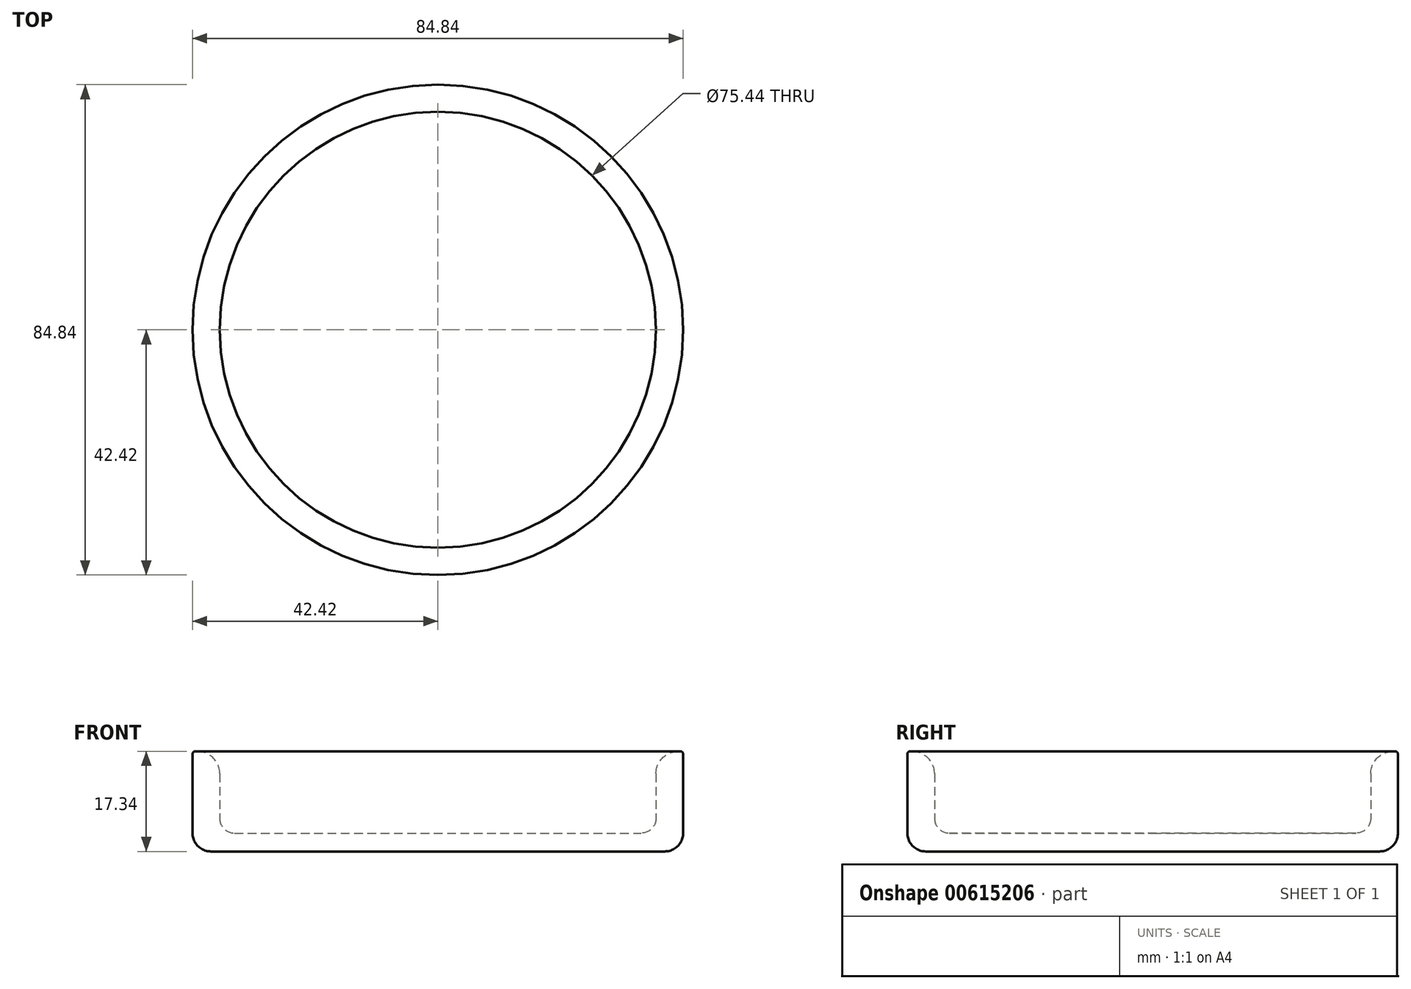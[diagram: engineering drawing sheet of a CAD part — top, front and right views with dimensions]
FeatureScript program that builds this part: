
annotation { "Feature Type Name" : "Feature", "Feature Type Description" : "" }
export const myFeature = defineFeature(function(context is Context, id is Id, definition is map)
    precondition{}
    {
        {
            var Q0;
            Q0=qCreatedBy(makeId("Front.planeOp"),FACE);
            var sketch = newSketch(context, id + "F0", { "sketchPlane" : qUnion([Q0])});
            skLineSegment(sketch, "E0", {"start": v(0, 0) * mm, "end": v(0, 3.18) * mm});
            skLineSegment(sketch, "E1", {"start": v(0, 3.18) * mm, "end": v(35.18, 3.18) * mm});
            skLineSegment(sketch, "E2", {"start": v(37.72, 5.72) * mm, "end": v(37.72, 13.47) * mm});
            skLineSegment(sketch, "E3", {"start": v(41.12, 17.26) * mm, "end": v(41.86, 17.34) * mm});
            skLineSegment(sketch, "E4", {"start": v(42.42, 16.83) * mm, "end": v(42.42, 3.18) * mm});
            skLineSegment(sketch, "E5", {"start": v(39.24, 0) * mm, "end": v(0, 0) * mm});
            skPoint(sketch, "E6.visualSharp", {"position": v(37.72, 3.18) * mm});
            skArc(sketch, "E6.filletArc", {"start": v(35.18, 3.18) * mm, "mid": v(36.98, 3.92) * mm, "end": v(37.72, 5.72) * mm});
            skPoint(sketch, "E7.visualSharp", {"position": v(37.72, 16.9) * mm});
            skArc(sketch, "E7.filletArc", {"start": v(41.12, 17.26) * mm, "mid": v(38.7, 16.02) * mm, "end": v(37.72, 13.47) * mm});
            skPoint(sketch, "E8.visualSharp", {"position": v(42.42, 17.4) * mm});
            skArc(sketch, "E8.filletArc", {"start": v(42.42, 16.83) * mm, "mid": v(42.25, 17.21) * mm, "end": v(41.86, 17.34) * mm});
            skPoint(sketch, "E9.visualSharp", {"position": v(42.42, 0) * mm});
            skArc(sketch, "E9.filletArc", {"start": v(39.24, 0) * mm, "mid": v(41.49, 0.93) * mm, "end": v(42.42, 3.18) * mm});
            skSolve(sketch);
        }
        {
            var Q0;
            Q0=makeQuery(id+"F0.imprint","IMPRINT",FACE,{"disambiguationData":[TD([[makeQuery(id+"F0.imprint","IMPRINT",EDGE,{"derivedFrom":sQuery(id+"F0.wireOp",EDGE,"E0")}),-1.0]])]});
            var Q1;
            Q1=sQuery(id+"F0.wireOp",EDGE,"E0");
            revolve(context, id + "F1", {"entities" : qUnion([Q0]), "axis" : qUnion([Q1]), "revolveType" : RevolveType.FULL});
        }
    });
